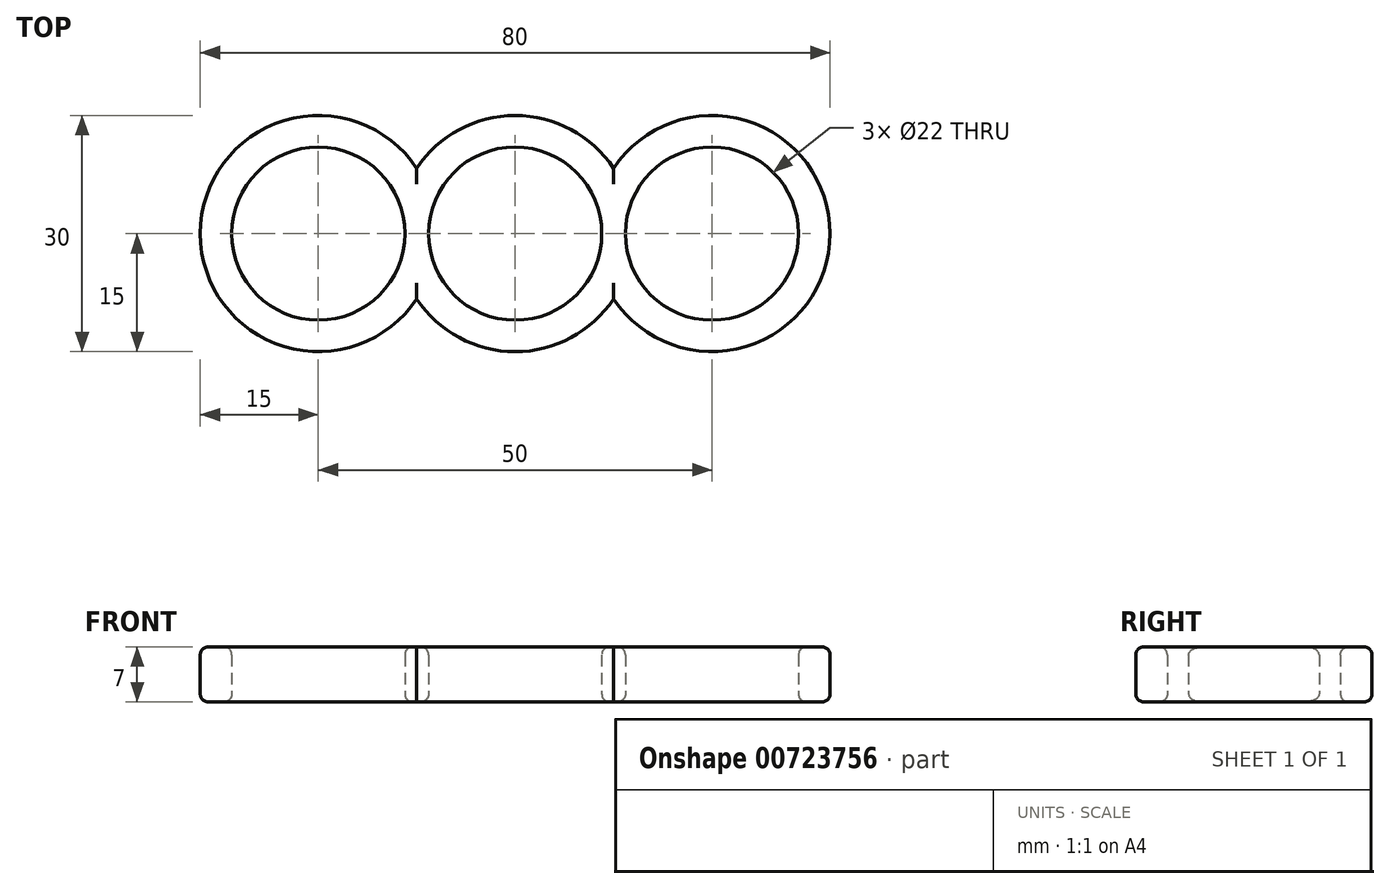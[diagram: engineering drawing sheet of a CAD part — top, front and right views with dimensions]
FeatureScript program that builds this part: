
annotation { "Feature Type Name" : "Feature", "Feature Type Description" : "" }
export const myFeature = defineFeature(function(context is Context, id is Id, definition is map)
    precondition{}
    {
        {
            var Q0;
            Q0=qCreatedBy(makeId("Top.planeOp"),FACE);
            var sketch = newSketch(context, id + "F0", { "sketchPlane" : qUnion([Q0])});
            skArc(sketch, "E0", {"start": v(0, 11) * mm, "mid": v(-11, 0) * mm, "end": v(0, -11) * mm});
            skArc(sketch, "E1", {"start": v(-12.5, -8.3) * mm, "mid": v(-7.1, -13.22) * mm, "end": v(0, -15) * mm});
            skCircle(sketch, "E2", {"center": v(-25, 0) * mm, "radius": 11 * mm});
            skArc(sketch, "E3", {"start": v(-12.5, 8.3) * mm, "mid": v(-40, 0) * mm, "end": v(-12.5, -8.3) * mm});
            skLineSegment(sketch, "E4", {"start": v(0, 15) * mm, "end": v(0, -15) * mm});
            skArc(sketch, "E5.trimOffspring", {"start": v(0, 15) * mm, "mid": v(-7.1, 13.22) * mm, "end": v(-12.5, 8.3) * mm});
            skArc(sketch, "E6.MirrorCS", {"start": v(12.5, -8.3) * mm, "mid": v(7.1, -13.22) * mm, "end": v(0, -15) * mm});
            skCircle(sketch, "E7.MirrorC", {"center": v(25, 0) * mm, "radius": 11 * mm});
            skArc(sketch, "E8.MirrorCS", {"start": v(0, 15) * mm, "mid": v(7.1, 13.22) * mm, "end": v(12.5, 8.3) * mm});
            skArc(sketch, "E9.MirrorCS", {"start": v(0, 11) * mm, "mid": v(11, 0) * mm, "end": v(0, -11) * mm});
            skArc(sketch, "E10.MirrorCS", {"start": v(12.5, 8.3) * mm, "mid": v(40, 0) * mm, "end": v(12.5, -8.3) * mm});
            skSolve(sketch);
        }
        {
            var Q0;
            Q0 = qSketchRegion(id + "F0", true);
            extrude(context, id + "F1", {"entities" : qUnion([Q0]), "depth" : 7 * mm, "offsetDistance" : 25.4 * mm});
        }
        {
            var Q0;
            Q0=makeQuery(id+"F1.opExtrude","CAP_FACE",FACE,{"disambiguationData":[OSD([sQuery(id+"F0.wireOp",EDGE,"E0"),sQuery(id+"F0.wireOp",EDGE,"E1"),sQuery(id+"F0.wireOp",EDGE,"E2"),sQuery(id+"F0.wireOp",EDGE,"E3"),sQuery(id+"F0.wireOp",EDGE,"E5.trimOffspring"),sQuery(id+"F0.wireOp",EDGE,"E6.MirrorCS"),sQuery(id+"F0.wireOp",EDGE,"E7.MirrorC"),sQuery(id+"F0.wireOp",EDGE,"E8.MirrorCS"),sQuery(id+"F0.wireOp",EDGE,"E9.MirrorCS"),sQuery(id+"F0.wireOp",EDGE,"E10.MirrorCS")])],"isStart":false});
            var Q1;
            Q1=makeQuery(id+"F1.opExtrude","CAP_FACE",FACE,{"disambiguationData":[OSD([sQuery(id+"F0.wireOp",EDGE,"E0"),sQuery(id+"F0.wireOp",EDGE,"E1"),sQuery(id+"F0.wireOp",EDGE,"E2"),sQuery(id+"F0.wireOp",EDGE,"E3"),sQuery(id+"F0.wireOp",EDGE,"E5.trimOffspring"),sQuery(id+"F0.wireOp",EDGE,"E6.MirrorCS"),sQuery(id+"F0.wireOp",EDGE,"E7.MirrorC"),sQuery(id+"F0.wireOp",EDGE,"E8.MirrorCS"),sQuery(id+"F0.wireOp",EDGE,"E9.MirrorCS"),sQuery(id+"F0.wireOp",EDGE,"E10.MirrorCS")])],"isStart":true});
            fillet(context, id + "F2", {"entities" : qUnion([Q0, Q1]), "radius" : 1 * mm, "tangentPropagation" : true, "allowEdgeOverflow" : false});
        }
    });
